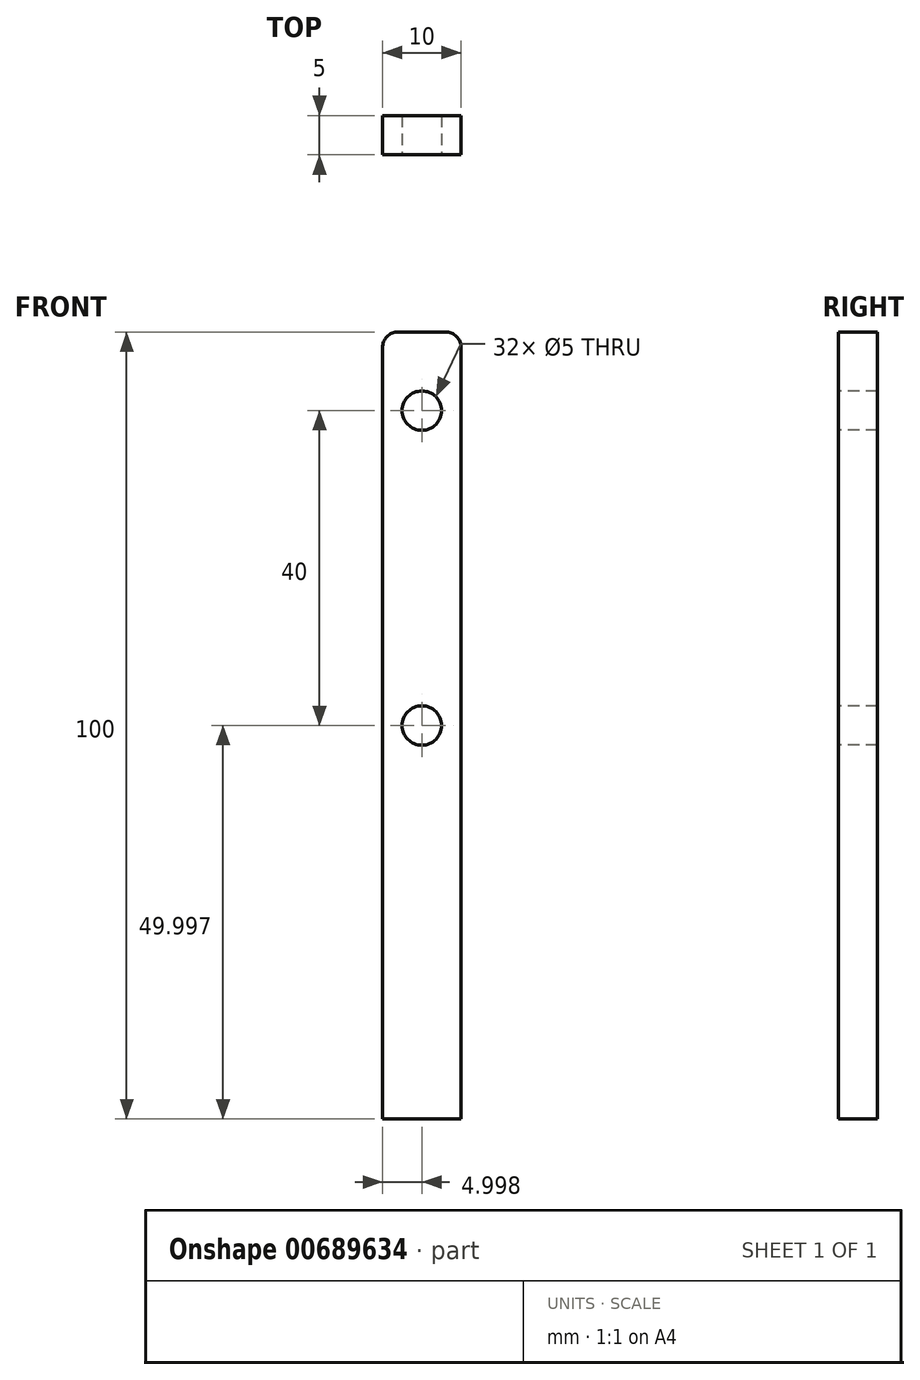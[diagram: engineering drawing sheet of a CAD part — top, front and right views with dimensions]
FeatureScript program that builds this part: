
annotation { "Feature Type Name" : "Feature", "Feature Type Description" : "" }
export const myFeature = defineFeature(function(context is Context, id is Id, definition is map)
    precondition{}
    {
        {
            var Q0;
            Q0=qCreatedBy(makeId("Front.planeOp"),FACE);
            var sketch = newSketch(context, id + "F0", { "sketchPlane" : qUnion([Q0])});
            skLineSegment(sketch, "E0.bottom", {"start": v(-13.8, 38.93) * mm, "end": v(-7.8, 38.93) * mm});
            skLineSegment(sketch, "E0.top", {"start": v(-15.8, -61.07) * mm, "end": v(-5.8, -61.07) * mm});
            skLineSegment(sketch, "E0.left", {"start": v(-15.8, 36.93) * mm, "end": v(-15.8, -61.07) * mm});
            skLineSegment(sketch, "E0.right", {"start": v(-5.8, 36.93) * mm, "end": v(-5.8, -61.07) * mm});
            skCircle(sketch, "E1", {"center": v(-10.8, -11.07) * mm, "radius": 2.5 * mm});
            skCircle(sketch, "E2", {"center": v(-10.8, 28.93) * mm, "radius": 2.5 * mm});
            skPoint(sketch, "E3.visualSharp", {"position": v(-15.8, 38.93) * mm});
            skArc(sketch, "E3.filletArc", {"start": v(-13.8, 38.93) * mm, "mid": v(-15.22, 38.34) * mm, "end": v(-15.8, 36.93) * mm});
            skPoint(sketch, "E4.visualSharp", {"position": v(-5.8, 38.93) * mm});
            skArc(sketch, "E4.filletArc", {"start": v(-5.8, 36.93) * mm, "mid": v(-6.39, 38.34) * mm, "end": v(-7.8, 38.93) * mm});
            skSolve(sketch);
        }
        {
            var Q0;
            Q0 = qSketchRegion(id + "F0", true);
            extrude(context, id + "F1", {"entities" : qUnion([Q0]), "oppositeDirection" : true, "depth" : 5 * mm, "offsetDistance" : 25 * mm});
        }
        {
            var Q0;
            Q0=makeQuery(id+"F0.imprint","IMPRINT",FACE,{"disambiguationData":[TD([[makeQuery(id+"F0.imprint","IMPRINT",EDGE,{"derivedFrom":sQuery(id+"F0.wireOp",EDGE,"E2")}),1.0]])]});
            extrude(context, id + "F2", {"entities" : qUnion([Q0]), "operationType" : NewBodyOperationType.REMOVE, "oppositeDirection" : true, "depth" : 5 * mm, "offsetDistance" : 25 * mm});
        }
        {
            var Q0;
            Q0=makeQuery(id+"F0.imprint","IMPRINT",FACE,{"disambiguationData":[TD([[makeQuery(id+"F0.imprint","IMPRINT",EDGE,{"derivedFrom":sQuery(id+"F0.wireOp",EDGE,"E1")}),1.0]])]});
            extrude(context, id + "F3", {"entities" : qUnion([Q0]), "operationType" : NewBodyOperationType.REMOVE, "oppositeDirection" : true, "depth" : 5 * mm, "offsetDistance" : 25 * mm});
        }
    });
